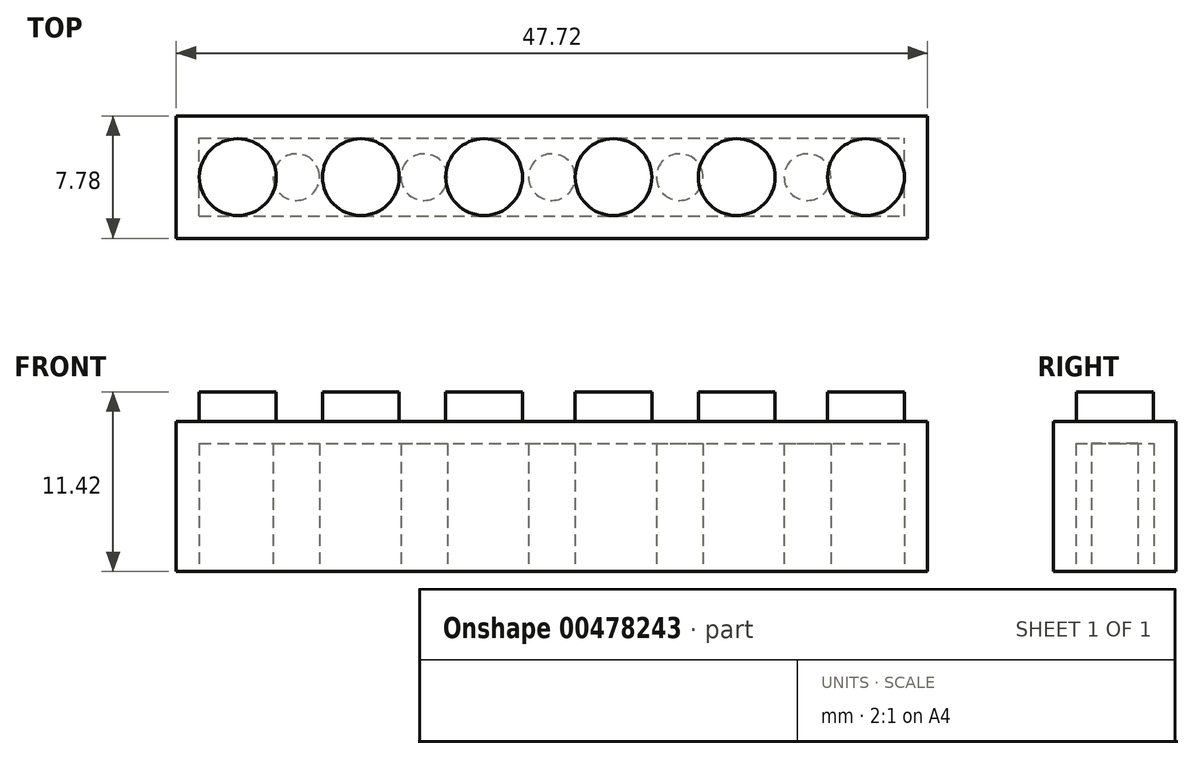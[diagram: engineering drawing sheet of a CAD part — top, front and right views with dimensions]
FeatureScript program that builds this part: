
annotation { "Feature Type Name" : "Feature", "Feature Type Description" : "" }
export const myFeature = defineFeature(function(context is Context, id is Id, definition is map)
    precondition{}
    {
        {
            var Q0;
            Q0=qCreatedBy(makeId("Top.planeOp"),FACE);
            var sketch = newSketch(context, id + "F0", { "sketchPlane" : qUnion([Q0])});
            skLineSegment(sketch, "E0.bottom", {"start": v(-23.86, 3.89) * mm, "end": v(23.86, 3.89) * mm});
            skLineSegment(sketch, "E0.top", {"start": v(-23.86, -3.89) * mm, "end": v(23.86, -3.89) * mm});
            skLineSegment(sketch, "E0.left", {"start": v(-23.86, 3.89) * mm, "end": v(-23.86, -3.89) * mm});
            skLineSegment(sketch, "E0.right", {"start": v(23.86, 3.89) * mm, "end": v(23.86, -3.89) * mm});
            skPoint(sketch, "E0.middle", {"position": v(0, 0) * mm});
            skSolve(sketch);
        }
        {
            var Q0;
            Q0=makeQuery(id+"F0.imprint","IMPRINT",FACE,{"disambiguationData":[TD([[makeQuery(id+"F0.imprint","IMPRINT",EDGE,{"derivedFrom":sQuery(id+"F0.wireOp",EDGE,"E0.bottom")}),-1.0]])]});
            extrude(context, id + "F1", {"entities" : qUnion([Q0]), "depth" : 9.52 * mm, "offsetDistance" : 25.4 * mm});
        }
        {
            var Q0;
            Q0=makeQuery(id+"F1.opExtrude","CAP_FACE",FACE,{"disambiguationData":[OSD([sQuery(id+"F0.wireOp",EDGE,"E0.bottom"),sQuery(id+"F0.wireOp",EDGE,"E0.top"),sQuery(id+"F0.wireOp",EDGE,"E0.left"),sQuery(id+"F0.wireOp",EDGE,"E0.right")])],"isStart":true});
            var sketch = newSketch(context, id + "F2", { "sketchPlane" : qUnion([Q0])});
            skLineSegment(sketch, "E1.bottom", {"start": v(-22.4, 2.48) * mm, "end": v(22.4, 2.48) * mm});
            skLineSegment(sketch, "E1.top", {"start": v(-22.4, -2.48) * mm, "end": v(22.4, -2.48) * mm});
            skLineSegment(sketch, "E1.left", {"start": v(-22.4, 2.48) * mm, "end": v(-22.4, -2.48) * mm});
            skLineSegment(sketch, "E1.right", {"start": v(22.4, 2.48) * mm, "end": v(22.4, -2.48) * mm});
            skPoint(sketch, "E1.middle", {"position": v(0, 0) * mm});
            skCircle(sketch, "E2", {"center": v(0, 0) * mm, "radius": 1.48 * mm});
            skCircle(sketch, "E3", {"center": v(-8.12, 0) * mm, "radius": 1.48 * mm});
            skCircle(sketch, "E4", {"center": v(-16.23, 0) * mm, "radius": 1.48 * mm});
            skCircle(sketch, "E5.MirrorC", {"center": v(8.12, 0) * mm, "radius": 1.48 * mm});
            skCircle(sketch, "E6.MirrorC", {"center": v(16.23, 0) * mm, "radius": 1.48 * mm});
            skSolve(sketch);
        }
        {
            var Q0;
            Q0=makeQuery(id+"F1.opExtrude","CAP_FACE",FACE,{"disambiguationData":[OSD([sQuery(id+"F0.wireOp",EDGE,"E0.bottom"),sQuery(id+"F0.wireOp",EDGE,"E0.top"),sQuery(id+"F0.wireOp",EDGE,"E0.left"),sQuery(id+"F0.wireOp",EDGE,"E0.right")])],"isStart":false});
            var sketch = newSketch(context, id + "F3", { "sketchPlane" : qUnion([Q0])});
            skCircle(sketch, "E7", {"center": v(-19.95, 0) * mm, "radius": 2.44 * mm});
            skCircle(sketch, "E8", {"center": v(-12.13, 0) * mm, "radius": 2.44 * mm});
            skCircle(sketch, "E9", {"center": v(-4.3, 0) * mm, "radius": 2.44 * mm});
            skCircle(sketch, "E10", {"center": v(3.91, 0) * mm, "radius": 2.44 * mm});
            skCircle(sketch, "E11", {"center": v(11.73, 0) * mm, "radius": 2.44 * mm});
            skCircle(sketch, "E12", {"center": v(19.95, 0) * mm, "radius": 2.44 * mm});
            skSolve(sketch);
        }
        {
            var Q0;
            Q0 = qSketchRegion(id + "F3", true);
            extrude(context, id + "F4", {"entities" : qUnion([Q0]), "operationType" : NewBodyOperationType.ADD, "depth" : 1.9 * mm, "offsetDistance" : 25.4 * mm});
        }
        {
            var Q0;
            Q0=makeQuery(id+"F2.imprint","IMPRINT",FACE,{"disambiguationData":[TD([[makeQuery(id+"F2.imprint","IMPRINT",EDGE,{"derivedFrom":sQuery(id+"F2.wireOp",EDGE,"E1.bottom")}),-1.0]])]});
            extrude(context, id + "F5", {"entities" : qUnion([Q0]), "operationType" : NewBodyOperationType.REMOVE, "oppositeDirection" : true, "depth" : 8.13 * mm, "offsetDistance" : 25.4 * mm});
        }
    });
